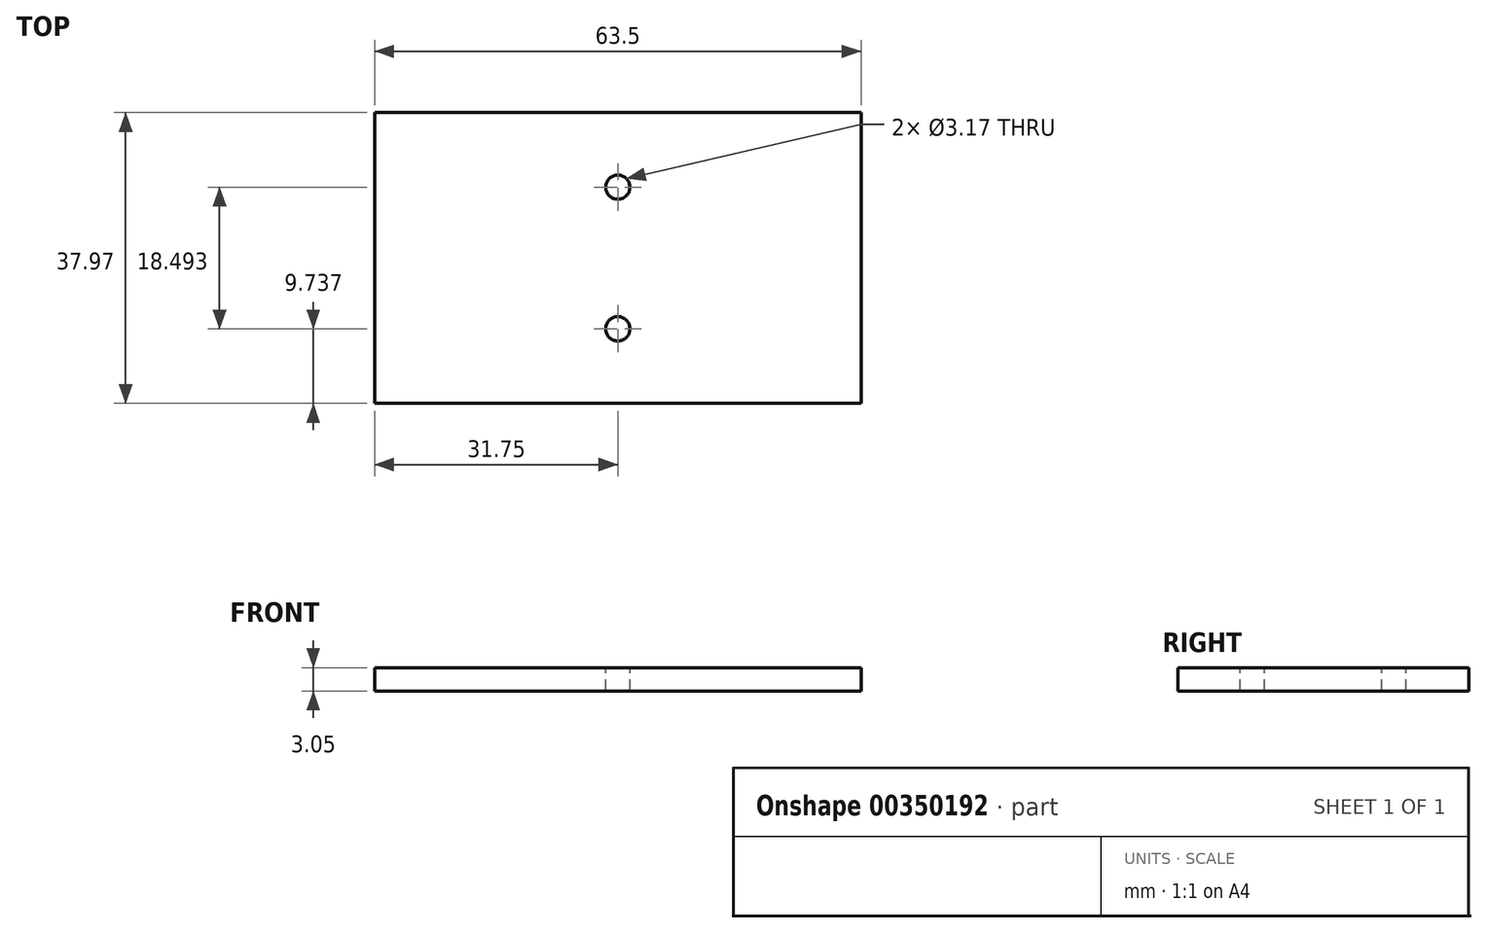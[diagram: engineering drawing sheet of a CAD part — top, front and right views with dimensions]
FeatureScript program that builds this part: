
annotation { "Feature Type Name" : "Feature", "Feature Type Description" : "" }
export const myFeature = defineFeature(function(context is Context, id is Id, definition is map)
    precondition{}
    {
        {
            var Q0;
            Q0=qCreatedBy(makeId("Top.planeOp"),FACE);
            var sketch = newSketch(context, id + "F0", { "sketchPlane" : qUnion([Q0])});
            skLineSegment(sketch, "E0.bottom", {"start": v(0, 0) * mm, "end": v(63.5, 0) * mm});
            skLineSegment(sketch, "E0.top", {"start": v(0, -37.97) * mm, "end": v(63.5, -37.97) * mm});
            skLineSegment(sketch, "E0.left", {"start": v(0, 0) * mm, "end": v(0, -37.97) * mm});
            skLineSegment(sketch, "E0.right", {"start": v(63.5, 0) * mm, "end": v(63.5, -37.97) * mm});
            skSolve(sketch);
        }
        {
            var Q0;
            Q0=makeQuery(id+"F0.imprint","IMPRINT",FACE,{"disambiguationData":[TD([[makeQuery(id+"F0.imprint","IMPRINT",EDGE,{"derivedFrom":sQuery(id+"F0.wireOp",EDGE,"E0.bottom")}),-1.0]])]});
            extrude(context, id + "F1", {"entities" : qUnion([Q0]), "depth" : 3.05 * mm});
        }
        {
            var Q0;
            Q0=makeQuery(id+"F1.opExtrude","CAP_FACE",FACE,{"disambiguationData":[OSD([sQuery(id+"F0.wireOp",EDGE,"E0.bottom"),sQuery(id+"F0.wireOp",EDGE,"E0.top"),sQuery(id+"F0.wireOp",EDGE,"E0.left"),sQuery(id+"F0.wireOp",EDGE,"E0.right")])],"isStart":false});
            var sketch = newSketch(context, id + "F2", { "sketchPlane" : qUnion([Q0])});
            skLineSegment(sketch, "E1", {"start": v(31.75, -37.97) * mm, "end": v(31.75, 0) * mm});
            skCircle(sketch, "E2", {"center": v(31.75, -28.23) * mm, "radius": 1.59 * mm});
            skLineSegment(sketch, "E3", {"start": v(0, -18.99) * mm, "end": v(63.5, -18.99) * mm});
            skCircle(sketch, "E4.MirrorC", {"center": v(31.75, -9.74) * mm, "radius": 1.59 * mm});
            skSolve(sketch);
        }
        {
            var Q0;
            Q0 = qSketchRegion(id + "F2", true);
            extrude(context, id + "F3", {"entities" : qUnion([Q0]), "operationType" : NewBodyOperationType.REMOVE, "endBound" : BoundingType.UP_TO_NEXT, "oppositeDirection" : true, "depth" : 25.4 * mm});
        }
    });
